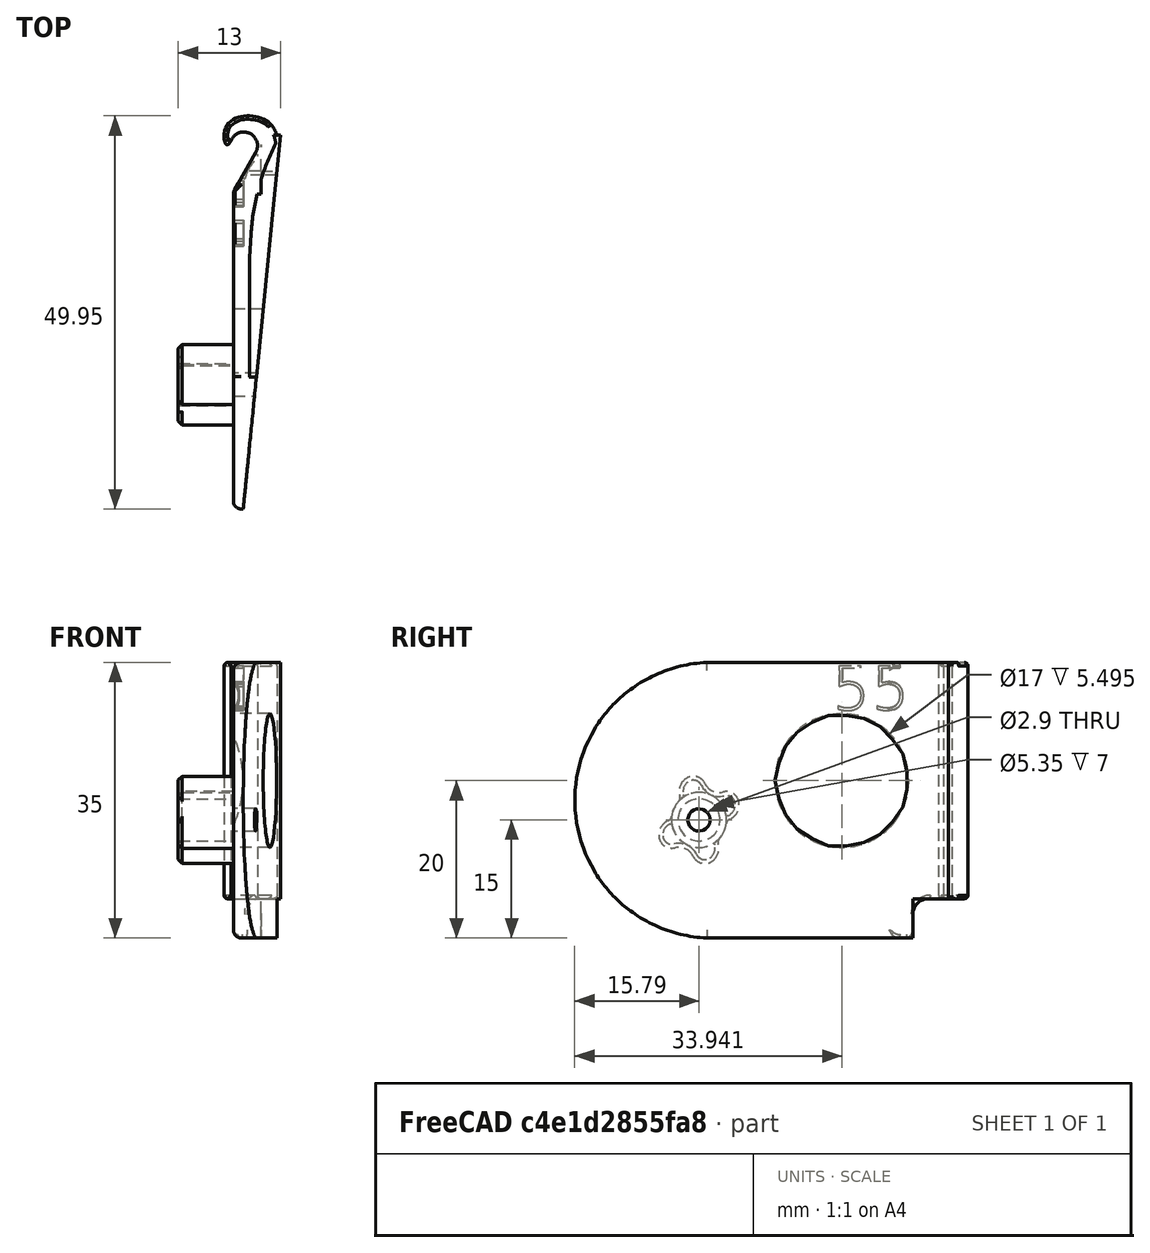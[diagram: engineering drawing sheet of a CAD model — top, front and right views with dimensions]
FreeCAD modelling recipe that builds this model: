
FCSTD DOCUMENT  (FreeCAD 0.18R)
Label: hinge-right-155deg-angled
License: All rights reserved
LicenseURL: http://en.wikipedia.org/wiki/All_rights_reserved
objects: App::FeaturePython×4, Part::FeaturePython×2, Part::Part2DObjectPython×1, Part::Extrusion×1, Part::Cut×1
note: 5 computed .brp shape members not serialized (recipe doc carries the construction recipe); baked Part::Feature solids carry a one-line shape summary decoded from their .brp

FEATURE [Part::FeaturePython] pillar_base_001  label="pillar-base_001"  # a2plus imported part (geometry in sourceFile) (typed FeaturePython)
  Placement = pos=(0.000608724,-56.4392,26.312) rot=(1,0,0;5.41069rad)
  a2p_Version = V0.1
  fixedPosition = false
  objectType = a2pPart
  sourceFile = ./parts/pillar-base.fcstd
  subassemblyImport = false
  timeLastImport = 1.60452e+09
  updateColors = true
FEATURE [Part::Part2DObjectPython] ShapeString  # Draft 2D object (typed FeaturePython)
  FontFile = <path>
  Placement = pos=(1.61,10.5,29) rot=(0.57735,-0.57735,-0.57735;2.0944rad)
  Size = 6
  String = 55
  Tracking = 0
FEATURE [Part::Extrusion] Extrude
  Base = -> ShapeString
  Dir = (-1,0,0)
  DirMode = 2
  FaceMakerClass = Part::FaceMakerBullseye
  LengthFwd = 3.5
  LengthRev = 0
  Placement = pos=(0,0,0) rot=(0,0,1;3.14159rad)
  Solid = false
  Symmetric = false
FEATURE [Part::FeaturePython] bracket_right_angled_001  label="bracket-right-angled_001"  # a2plus imported part (geometry in sourceFile) (typed FeaturePython)
  Placement = pos=(0,0,0) rot=(0,0,1;3.14159rad)
  a2p_Version = V0.1
  fixedPosition = true
  objectType = a2pPart
  sourceFile = ./parts/bracket-right-angled.fcstd
  subassemblyImport = false
  timeLastImport = 1.60454e+09
  updateColors = true
FEATURE [App::FeaturePython] axisCoincident_001  label="axisCoincident_001__bracket-right-angled_001"  # a2plus constraint (typed FeaturePython)
  Object1 = pillar_base_001
  Object2 = bracket_right_angled_001
  ParentTreeObject = -> pillar_base_001
  SubElement1 = Face17
  SubElement2 = Face27
  Suppressed = false
  Type = axial
  directionConstraint = 1
  lockRotation = false
FEATURE [App::FeaturePython] axisCoincident_001_mirror  label="axisCoincident_001__pillar-base_001"  # a2plus constraint (typed FeaturePython)
  Object1 = pillar_base_001
  Object2 = bracket_right_angled_001
  ParentTreeObject = -> bracket_right_angled_001
  SubElement1 = Face17
  SubElement2 = Face27
  Suppressed = false
  Type = axial
  directionConstraint = 1
  lockRotation = false
FEATURE [App::FeaturePython] planeCoincident_001  label="planeCoincident_001__bracket-right-angled_001"  # a2plus constraint (typed FeaturePython)
  Object1 = pillar_base_001
  Object2 = bracket_right_angled_001
  ParentTreeObject = -> pillar_base_001
  SubElement1 = Face1
  SubElement2 = Face55
  Suppressed = false
  Type = plane
  directionConstraint = 1
  offset = 0
FEATURE [App::FeaturePython] planeCoincident_001_mirror  label="planeCoincident_001__pillar-base_001"  # a2plus constraint (typed FeaturePython)
  Object1 = pillar_base_001
  Object2 = bracket_right_angled_001
  ParentTreeObject = -> bracket_right_angled_001
  SubElement1 = Face1
  SubElement2 = Face55
  Suppressed = false
  Type = plane
  directionConstraint = 1
  offset = 0
FEATURE [Part::Cut] Cut
  Base = -> bracket_right_angled_001
  Tool = -> Extrude
note: 1 file-system path scrubbed to <path> (originals preserved in the JSON sidecar)
